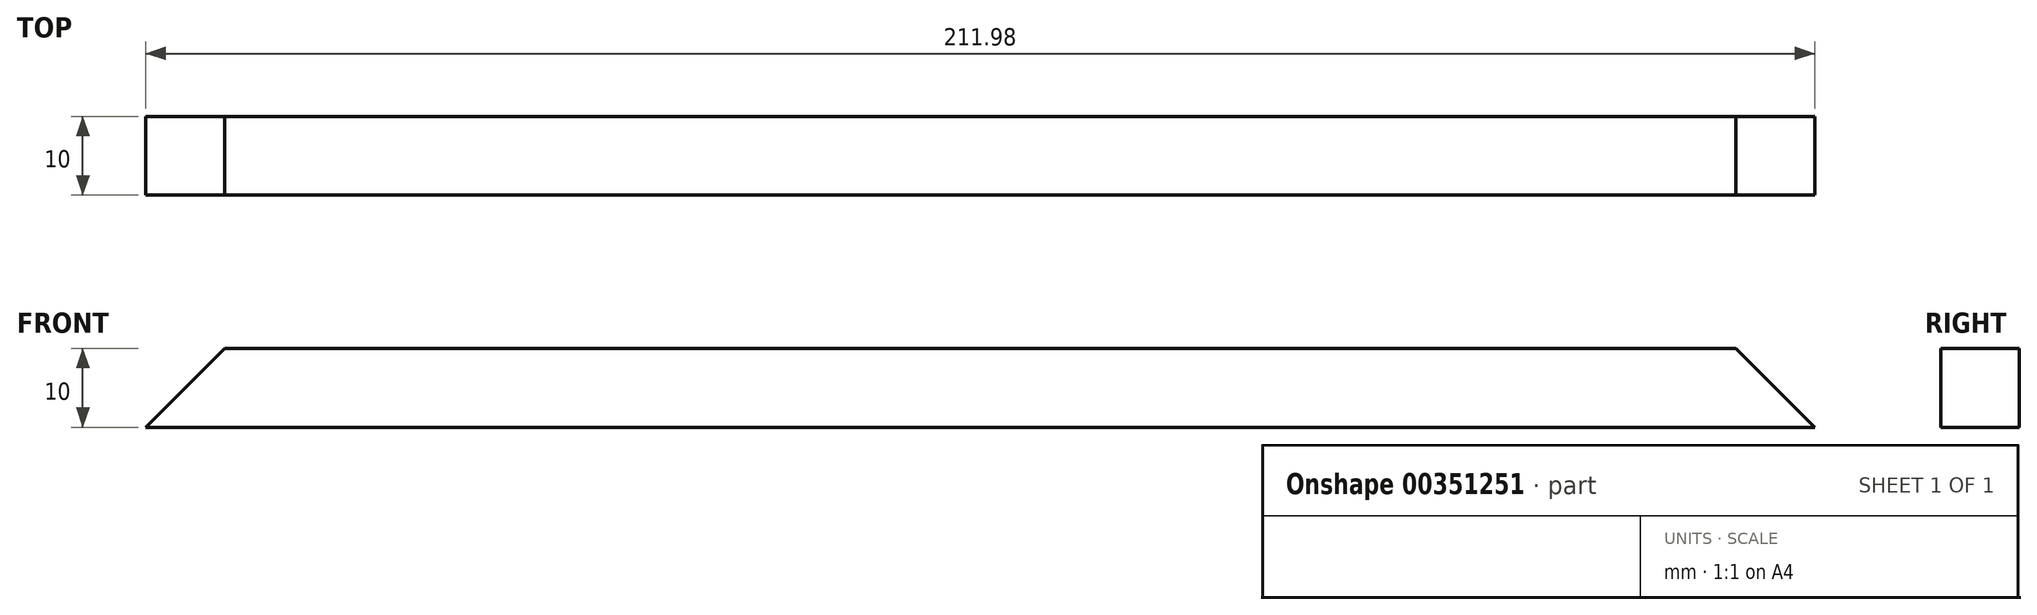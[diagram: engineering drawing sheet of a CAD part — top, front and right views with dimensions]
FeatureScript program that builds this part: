
annotation { "Feature Type Name" : "Feature", "Feature Type Description" : "" }
export const myFeature = defineFeature(function(context is Context, id is Id, definition is map)
    precondition{}
    {
        {
            var Q0;
            Q0=qCreatedBy(makeId("Front.planeOp"),FACE);
            var sketch = newSketch(context, id + "F0", { "sketchPlane" : qUnion([Q0])});
            skLineSegment(sketch, "E0.bottom", {"start": v(-70.42, -3.09) * mm, "end": v(141.56, -3.09) * mm});
            skLineSegment(sketch, "E0.top", {"start": v(-70.42, -13.09) * mm, "end": v(141.56, -13.09) * mm});
            skLineSegment(sketch, "E0.left", {"start": v(-70.42, -3.09) * mm, "end": v(-70.42, -13.09) * mm});
            skLineSegment(sketch, "E0.right", {"start": v(141.56, -3.09) * mm, "end": v(141.56, -13.09) * mm});
            skSolve(sketch);
        }
        {
            var Q0;
            Q0=makeQuery(id+"F0.imprint","IMPRINT",FACE,{"disambiguationData":[TD([[makeQuery(id+"F0.imprint","IMPRINT",EDGE,{"derivedFrom":sQuery(id+"F0.wireOp",EDGE,"E0.bottom")}),-1.0]])]});
            extrude(context, id + "F1", {"entities" : qUnion([Q0]), "depth" : 10 * mm});
        }
        {
            var Q0;
            Q0=makeQuery(id+"F1.opExtrude","SWEPT_EDGE",EDGE,{"disambiguationData":[OSD([sQuery(id+"F0.wireOp",EDGE,"E0.bottom"),sQuery(id+"F0.wireOp",EDGE,"E0.right")])]});
            chamfer(context, id + "F2", {"entities" : qUnion([Q0]), "width" : 10 * mm, "tangentPropagation" : true});
        }
        {
            var Q0;
            Q0=makeQuery(id+"F1.opExtrude","SWEPT_EDGE",EDGE,{"disambiguationData":[OSD([sQuery(id+"F0.wireOp",EDGE,"E0.bottom"),sQuery(id+"F0.wireOp",EDGE,"E0.left")])]});
            chamfer(context, id + "F3", {"entities" : qUnion([Q0]), "width" : 10 * mm, "tangentPropagation" : true});
        }
    });
